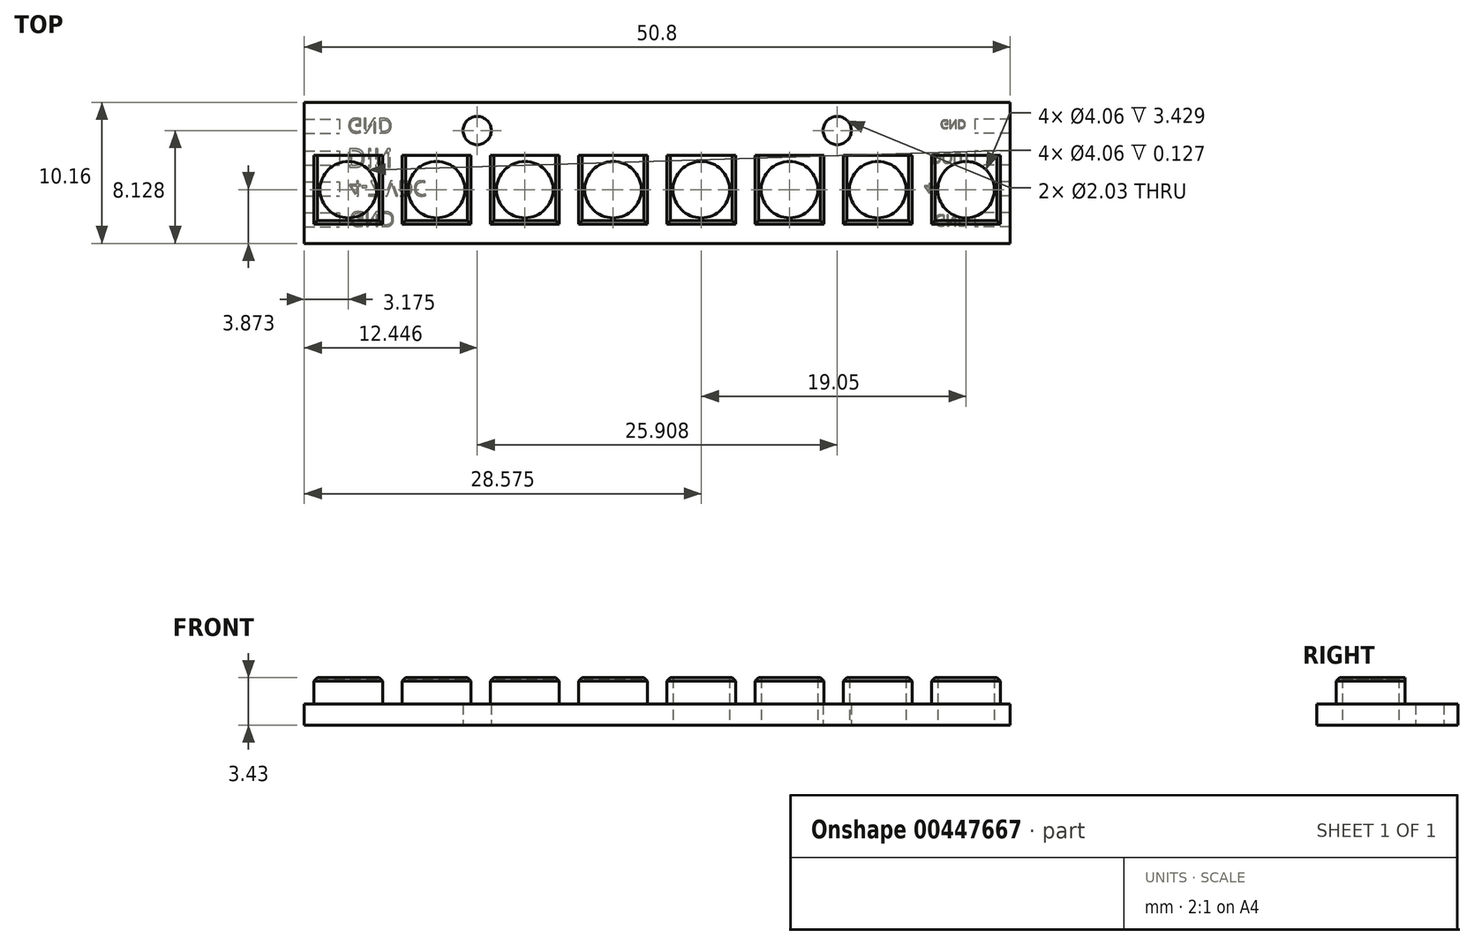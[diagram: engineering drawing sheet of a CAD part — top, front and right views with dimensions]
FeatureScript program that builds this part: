
annotation { "Feature Type Name" : "Feature", "Feature Type Description" : "" }
export const myFeature = defineFeature(function(context is Context, id is Id, definition is map)
    precondition{}
    {
        {
            var Q0;
            Q0=qCreatedBy(makeId("Top.planeOp"),FACE);
            var sketch = newSketch(context, id + "F0", { "sketchPlane" : qUnion([Q0])});
            skLineSegment(sketch, "E0.bottom", {"start": v(25.4, 5.08) * mm, "end": v(-25.4, 5.08) * mm});
            skLineSegment(sketch, "E0.top", {"start": v(25.4, -5.08) * mm, "end": v(-25.4, -5.08) * mm});
            skLineSegment(sketch, "E0.left", {"start": v(25.4, 5.08) * mm, "end": v(25.4, -5.08) * mm});
            skLineSegment(sketch, "E0.right", {"start": v(-25.4, 5.08) * mm, "end": v(-25.4, -5.08) * mm});
            skPoint(sketch, "E0.middle", {"position": v(0, 0) * mm});
            skCircle(sketch, "E1", {"center": v(-12.95, 3.05) * mm, "radius": 1.02 * mm});
            skLineSegment(sketch, "E2", {"start": v(-25.4, 1.27) * mm, "end": v(25.4, 1.27) * mm});
            skLineSegment(sketch, "E3.bottom", {"start": v(-25.4, 1.27) * mm, "end": v(-19.75, 1.27) * mm});
            skLineSegment(sketch, "E3.left", {"start": v(-25.4, 1.27) * mm, "end": v(-25.4, -3.68) * mm});
            skLineSegment(sketch, "E3.right", {"start": v(-19.75, 1.27) * mm, "end": v(-19.75, -3.68) * mm});
            skLineSegment(sketch, "E4.bottom", {"start": v(-18.35, 1.27) * mm, "end": v(-13.4, 1.27) * mm});
            skLineSegment(sketch, "E4.top", {"start": v(-18.35, -3.68) * mm, "end": v(-13.4, -3.68) * mm});
            skLineSegment(sketch, "E4.left", {"start": v(-18.35, 1.27) * mm, "end": v(-18.35, -3.68) * mm});
            skLineSegment(sketch, "E4.right", {"start": v(-13.4, 1.27) * mm, "end": v(-13.4, -3.68) * mm});
            skLineSegment(sketch, "E5.bottom", {"start": v(-12, 1.27) * mm, "end": v(-7.05, 1.27) * mm});
            skLineSegment(sketch, "E5.top", {"start": v(-12, -3.68) * mm, "end": v(-7.05, -3.68) * mm});
            skLineSegment(sketch, "E5.left", {"start": v(-12, 1.27) * mm, "end": v(-12, -3.68) * mm});
            skLineSegment(sketch, "E5.right", {"start": v(-7.05, 1.27) * mm, "end": v(-7.05, -3.68) * mm});
            skPoint(sketch, "E6.oppositeSnap0", {"position": v(-9.53, -3.68) * mm});
            skLineSegment(sketch, "E6.bottom", {"start": v(-5.65, 1.27) * mm, "end": v(-0.7, 1.27) * mm});
            skLineSegment(sketch, "E6.top", {"start": v(-5.65, -3.68) * mm, "end": v(-0.7, -3.68) * mm});
            skLineSegment(sketch, "E6.left", {"start": v(-5.65, 1.27) * mm, "end": v(-5.65, -3.68) * mm});
            skLineSegment(sketch, "E6.right", {"start": v(-0.7, 1.27) * mm, "end": v(-0.7, -3.68) * mm});
            skCircle(sketch, "E7.MirrorC", {"center": v(12.95, 3.05) * mm, "radius": 1.02 * mm});
            skLineSegment(sketch, "E8.MirrorCS", {"start": v(18.35, -3.68) * mm, "end": v(13.4, -3.68) * mm});
            skLineSegment(sketch, "E9.MirrorCS", {"start": v(13.4, 1.27) * mm, "end": v(13.4, -3.68) * mm});
            skLineSegment(sketch, "E10.MirrorCS", {"start": v(18.35, 1.27) * mm, "end": v(18.35, -3.68) * mm});
            skLineSegment(sketch, "E11.MirrorCS", {"start": v(18.35, 1.27) * mm, "end": v(13.4, 1.27) * mm});
            skLineSegment(sketch, "E12.MirrorCS", {"start": v(19.75, 1.27) * mm, "end": v(19.75, -3.68) * mm});
            skLineSegment(sketch, "E13.MirrorCS", {"start": v(25.4, 1.27) * mm, "end": v(19.75, 1.27) * mm});
            skLineSegment(sketch, "E14.MirrorCS", {"start": v(25.4, 1.27) * mm, "end": v(-25.4, 1.27) * mm});
            skLineSegment(sketch, "E15.MirrorCS", {"start": v(12, 1.27) * mm, "end": v(12, -3.68) * mm});
            skLineSegment(sketch, "E16.MirrorCS", {"start": v(12, -3.68) * mm, "end": v(7.05, -3.68) * mm});
            skLineSegment(sketch, "E17.MirrorCS", {"start": v(7.05, 1.27) * mm, "end": v(7.05, -3.68) * mm});
            skLineSegment(sketch, "E18.MirrorCS", {"start": v(5.65, 1.27) * mm, "end": v(5.65, -3.68) * mm});
            skLineSegment(sketch, "E19.MirrorCS", {"start": v(5.65, 1.27) * mm, "end": v(0.7, 1.27) * mm});
            skLineSegment(sketch, "E20.MirrorCS", {"start": v(5.65, -3.68) * mm, "end": v(0.7, -3.68) * mm});
            skLineSegment(sketch, "E21.MirrorCS", {"start": v(0.7, 1.27) * mm, "end": v(0.7, -3.68) * mm});
            skPoint(sketch, "E22.centerSnap0", {"position": v(-15.88, 1.27) * mm});
            skPoint(sketch, "E23.centerSnap0", {"position": v(-9.53, 1.27) * mm});
            skPoint(sketch, "E24.centerSnap0", {"position": v(-3.18, 1.27) * mm});
            skLineSegment(sketch, "E25", {"start": v(-24.7, 1.27) * mm, "end": v(-24.7, -3.68) * mm});
            skLineSegment(sketch, "E26.MirrorCS", {"start": v(24.7, 1.27) * mm, "end": v(24.7, -3.68) * mm});
            skLineSegment(sketch, "E27", {"start": v(24.7, -3.68) * mm, "end": v(19.75, -3.68) * mm});
            skLineSegment(sketch, "E28", {"start": v(-24.7, -3.68) * mm, "end": v(-19.75, -3.68) * mm});
            skCircle(sketch, "E29", {"center": v(-22.23, -1.2) * mm, "radius": 2.03 * mm});
            skCircle(sketch, "E30", {"center": v(-15.88, -1.2) * mm, "radius": 2.03 * mm});
            skCircle(sketch, "E31", {"center": v(-9.53, -1.2) * mm, "radius": 2.03 * mm});
            skCircle(sketch, "E32", {"center": v(-3.18, -1.2) * mm, "radius": 2.03 * mm});
            skCircle(sketch, "E33.MirrorC", {"center": v(3.18, -1.2) * mm, "radius": 2.03 * mm});
            skCircle(sketch, "E34.MirrorC", {"center": v(9.53, -1.2) * mm, "radius": 2.03 * mm});
            skCircle(sketch, "E35.MirrorC", {"center": v(15.88, -1.2) * mm, "radius": 2.03 * mm});
            skCircle(sketch, "E36.MirrorC", {"center": v(22.23, -1.2) * mm, "radius": 2.03 * mm});
            skSolve(sketch);
        }
        {
            var Q0;
            {var subQ15=sQuery(id+"F0.wireOp",EDGE,"E0.bottom");Q0=makeQuery(id+"F0.imprint","IMPRINT",FACE,{"disambiguationData":[TD([[makeQuery(id+"F0.imprint","IMPRINT",EDGE,{"derivedFrom":subQ15}),1.0]])]});}
            var Q1;
            Q1=makeQuery(id+"F0.imprint","IMPRINT",FACE,{"disambiguationData":[TD([[makeQuery(id+"F0.imprint","IMPRINT",EDGE,{"derivedFrom":sQuery(id+"F0.wireOp",EDGE,"E5.top")}),1.0]])]});
            var Q2;
            Q2=makeQuery(id+"F0.imprint","IMPRINT",FACE,{"disambiguationData":[TD([[makeQuery(id+"F0.imprint","IMPRINT",EDGE,{"derivedFrom":sQuery(id+"F0.wireOp",EDGE,"E4.top")}),1.0]])]});
            var Q3;
            Q3=makeQuery(id+"F0.imprint","IMPRINT",FACE,{"disambiguationData":[TD([[makeQuery(id+"F0.imprint","IMPRINT",EDGE,{"derivedFrom":sQuery(id+"F0.wireOp",EDGE,"E3.top")}),1.0]])]});
            var Q4;
            Q4=makeQuery(id+"F0.imprint","IMPRINT",FACE,{"disambiguationData":[TD([[makeQuery(id+"F0.imprint","IMPRINT",EDGE,{"derivedFrom":sQuery(id+"F0.wireOp",EDGE,"E6.top")}),1.0]])]});
            var Q5;
            Q5=makeQuery(id+"F0.imprint","IMPRINT",FACE,{"disambiguationData":[TD([[makeQuery(id+"F0.imprint","IMPRINT",EDGE,{"derivedFrom":sQuery(id+"F0.wireOp",EDGE,"E18.MirrorCS")}),-1.0]])]});
            var Q6;
            {var subQ0=sQuery(id+"F0.wireOp",EDGE,"E15.MirrorCS");Q6=makeQuery(id+"F0.imprint","IMPRINT",FACE,{"disambiguationData":[TD([[makeQuery(id+"F0.imprint","IMPRINT",EDGE,{"derivedFrom":subQ0}),-1.0]])]});}
            var Q7;
            Q7=makeQuery(id+"F0.imprint","IMPRINT",FACE,{"disambiguationData":[TD([[makeQuery(id+"F0.imprint","IMPRINT",EDGE,{"derivedFrom":sQuery(id+"F0.wireOp",EDGE,"E8.MirrorCS")}),-1.0]])]});
            var Q8;
            {var subQ4=sQuery(id+"F0.wireOp",EDGE,"E12.MirrorCS");Q8=makeQuery(id+"F0.imprint","IMPRINT",FACE,{"disambiguationData":[TD([[makeQuery(id+"F0.imprint","IMPRINT",EDGE,{"derivedFrom":subQ4}),1.0]])]});}
            var Q9;
            {var subQ0=sQuery(id+"F0.wireOp",EDGE,"E22");var subQ1=makeQuery(id+"F0.imprint","INTERSECT",VERTEX,{"derivedFrom":[sQuery(id+"F0.wireOp",EDGE,"E4.right"),subQ0]});Q9=makeQuery(id+"F0.imprint","IMPRINT",FACE,{"disambiguationData":[TD([[makeQuery(id+"F0.imprint","IMPRINT",EDGE,{"disambiguationData":[TD([[subQ1,-1.0]])],"derivedFrom":subQ0}),1.0]])]});}
            var Q10;
            {var subQ0=sQuery(id+"F0.wireOp",EDGE,"UNAH1sZw-Ke5a-9nqM-yAOw-CyViDykzE4hE");var subQ1=makeQuery(id+"F0.imprint","INTERSECT",VERTEX,{"derivedFrom":[sQuery(id+"F0.wireOp",EDGE,"E3.right"),subQ0]});Q10=makeQuery(id+"F0.imprint","IMPRINT",FACE,{"disambiguationData":[TD([[makeQuery(id+"F0.imprint","IMPRINT",EDGE,{"disambiguationData":[TD([[subQ1,-1.0]])],"derivedFrom":subQ0}),1.0]])]});}
            var Q11;
            {var subQ1=sQuery(id+"F0.wireOp",EDGE,"E3.left");var subQ3=sQuery(id+"F0.wireOp",EDGE,"UNAH1sZw-Ke5a-9nqM-yAOw-CyViDykzE4hE");var subQ4=makeQuery(id+"F0.imprint","INTERSECT",VERTEX,{"derivedFrom":[subQ1,subQ3]});Q11=makeQuery(id+"F0.imprint","IMPRINT",FACE,{"disambiguationData":[TD([[makeQuery(id+"F0.imprint","IMPRINT",EDGE,{"disambiguationData":[TD([[subQ4,1.0]])],"derivedFrom":subQ3}),-1.0]])]});}
            var Q12;
            {var subQ0=sQuery(id+"F0.wireOp",EDGE,"E14.MirrorCS");var subQ1=sQuery(id+"F0.wireOp",EDGE,"E3.right");var subQ2=makeQuery(id+"F0.imprint","INTERSECT",VERTEX,{"derivedFrom":[subQ1,subQ0]});Q12=makeQuery(id+"F0.imprint","IMPRINT",FACE,{"disambiguationData":[TD([[makeQuery(id+"F0.imprint","IMPRINT",EDGE,{"disambiguationData":[TD([[subQ2,-1.0]])],"derivedFrom":subQ1}),-1.0]])]});}
            var Q13;
            {var subQ0=sQuery(id+"F0.wireOp",EDGE,"E14.MirrorCS");var subQ1=sQuery(id+"F0.wireOp",EDGE,"E4.left");var subQ2=makeQuery(id+"F0.imprint","INTERSECT",VERTEX,{"derivedFrom":[subQ1,subQ0]});Q13=makeQuery(id+"F0.imprint","IMPRINT",FACE,{"disambiguationData":[TD([[makeQuery(id+"F0.imprint","IMPRINT",EDGE,{"disambiguationData":[TD([[subQ2,-1.0]])],"derivedFrom":subQ1}),1.0]])]});}
            var Q14;
            {var subQ52=sQuery(id+"F0.wireOp",EDGE,"E0.top");Q14=makeQuery(id+"F0.imprint","IMPRINT",FACE,{"disambiguationData":[TD([[makeQuery(id+"F0.imprint","IMPRINT",EDGE,{"derivedFrom":subQ52}),-1.0]])]});}
            var Q15;
            {var subQ0=sQuery(id+"F0.wireOp",EDGE,"E14.MirrorCS");var subQ1=sQuery(id+"F0.wireOp",EDGE,"E4.right");var subQ2=makeQuery(id+"F0.imprint","INTERSECT",VERTEX,{"derivedFrom":[subQ1,subQ0]});Q15=makeQuery(id+"F0.imprint","IMPRINT",FACE,{"disambiguationData":[TD([[makeQuery(id+"F0.imprint","IMPRINT",EDGE,{"disambiguationData":[TD([[subQ2,-1.0]])],"derivedFrom":subQ1}),-1.0]])]});}
            var Q16;
            {var subQ0=sQuery(id+"F0.wireOp",EDGE,"E23");var subQ1=makeQuery(id+"F0.imprint","INTERSECT",VERTEX,{"derivedFrom":[sQuery(id+"F0.wireOp",EDGE,"E5.right"),subQ0]});Q16=makeQuery(id+"F0.imprint","IMPRINT",FACE,{"disambiguationData":[TD([[makeQuery(id+"F0.imprint","IMPRINT",EDGE,{"disambiguationData":[TD([[subQ1,-1.0]])],"derivedFrom":subQ0}),1.0]])]});}
            var Q17;
            {var subQ0=sQuery(id+"F0.wireOp",EDGE,"E14.MirrorCS");var subQ1=sQuery(id+"F0.wireOp",EDGE,"E5.left");var subQ2=makeQuery(id+"F0.imprint","INTERSECT",VERTEX,{"derivedFrom":[subQ1,subQ0]});Q17=makeQuery(id+"F0.imprint","IMPRINT",FACE,{"disambiguationData":[TD([[makeQuery(id+"F0.imprint","IMPRINT",EDGE,{"disambiguationData":[TD([[subQ2,-1.0]])],"derivedFrom":subQ1}),1.0]])]});}
            var Q18;
            {var subQ0=sQuery(id+"F0.wireOp",EDGE,"E14.MirrorCS");var subQ1=sQuery(id+"F0.wireOp",EDGE,"E5.right");var subQ2=makeQuery(id+"F0.imprint","INTERSECT",VERTEX,{"derivedFrom":[subQ1,subQ0]});Q18=makeQuery(id+"F0.imprint","IMPRINT",FACE,{"disambiguationData":[TD([[makeQuery(id+"F0.imprint","IMPRINT",EDGE,{"disambiguationData":[TD([[subQ2,-1.0]])],"derivedFrom":subQ1}),-1.0]])]});}
            var Q19;
            {var subQ0=sQuery(id+"F0.wireOp",EDGE,"E24");var subQ1=makeQuery(id+"F0.imprint","INTERSECT",VERTEX,{"derivedFrom":[sQuery(id+"F0.wireOp",EDGE,"E6.right"),subQ0]});Q19=makeQuery(id+"F0.imprint","IMPRINT",FACE,{"disambiguationData":[TD([[makeQuery(id+"F0.imprint","IMPRINT",EDGE,{"disambiguationData":[TD([[subQ1,-1.0]])],"derivedFrom":subQ0}),1.0]])]});}
            var Q20;
            {var subQ0=sQuery(id+"F0.wireOp",EDGE,"E14.MirrorCS");var subQ1=sQuery(id+"F0.wireOp",EDGE,"E6.left");var subQ2=makeQuery(id+"F0.imprint","INTERSECT",VERTEX,{"derivedFrom":[subQ1,subQ0]});Q20=makeQuery(id+"F0.imprint","IMPRINT",FACE,{"disambiguationData":[TD([[makeQuery(id+"F0.imprint","IMPRINT",EDGE,{"disambiguationData":[TD([[subQ2,-1.0]])],"derivedFrom":subQ1}),1.0]])]});}
            var Q21;
            {var subQ0=sQuery(id+"F0.wireOp",EDGE,"E14.MirrorCS");var subQ1=sQuery(id+"F0.wireOp",EDGE,"E6.right");var subQ2=makeQuery(id+"F0.imprint","INTERSECT",VERTEX,{"derivedFrom":[subQ1,subQ0]});Q21=makeQuery(id+"F0.imprint","IMPRINT",FACE,{"disambiguationData":[TD([[makeQuery(id+"F0.imprint","IMPRINT",EDGE,{"disambiguationData":[TD([[subQ2,-1.0]])],"derivedFrom":subQ1}),-1.0]])]});}
            var Q22;
            {var subQ0=sQuery(id+"F0.wireOp",EDGE,"8c9498a9-89d4-41b4-a61f-fcb31b3f8e1a0.MirrorC");var subQ1=makeQuery(id+"F0.imprint","INTERSECT",VERTEX,{"derivedFrom":[sQuery(id+"F0.wireOp",EDGE,"E19.MirrorCS"),subQ0]});Q22=makeQuery(id+"F0.imprint","IMPRINT",FACE,{"disambiguationData":[TD([[makeQuery(id+"F0.imprint","IMPRINT",EDGE,{"disambiguationData":[TD([[subQ1,1.0]])],"derivedFrom":subQ0}),-1.0]])]});}
            var Q23;
            {var subQ0=sQuery(id+"F0.wireOp",EDGE,"724678bf-c758-4b2b-ac49-fb71572171400.MirrorC");var subQ1=makeQuery(id+"F0.imprint","INTERSECT",VERTEX,{"derivedFrom":[sQuery(id+"F0.wireOp",EDGE,"E14.MirrorCS"),subQ0]});Q23=makeQuery(id+"F0.imprint","IMPRINT",FACE,{"disambiguationData":[TD([[makeQuery(id+"F0.imprint","IMPRINT",EDGE,{"disambiguationData":[TD([[subQ1,1.0]])],"derivedFrom":subQ0}),-1.0]])]});}
            var Q24;
            {var subQ0=sQuery(id+"F0.wireOp",EDGE,"96d1a491-8e30-4fa4-92a3-82973c83916c0.MirrorC");var subQ1=makeQuery(id+"F0.imprint","INTERSECT",VERTEX,{"derivedFrom":[sQuery(id+"F0.wireOp",EDGE,"E9.MirrorCS"),subQ0]});Q24=makeQuery(id+"F0.imprint","IMPRINT",FACE,{"disambiguationData":[TD([[makeQuery(id+"F0.imprint","IMPRINT",EDGE,{"disambiguationData":[TD([[subQ1,-1.0]])],"derivedFrom":subQ0}),-1.0]])]});}
            var Q25;
            {var subQ0=sQuery(id+"F0.wireOp",EDGE,"E14.MirrorCS");var subQ1=sQuery(id+"F0.wireOp",EDGE,"E9.MirrorCS");var subQ2=makeQuery(id+"F0.imprint","INTERSECT",VERTEX,{"derivedFrom":[subQ1,subQ0]});Q25=makeQuery(id+"F0.imprint","IMPRINT",FACE,{"disambiguationData":[TD([[makeQuery(id+"F0.imprint","IMPRINT",EDGE,{"disambiguationData":[TD([[subQ2,-1.0]])],"derivedFrom":subQ1}),1.0]])]});}
            var Q26;
            {var subQ0=sQuery(id+"F0.wireOp",EDGE,"E14.MirrorCS");var subQ1=sQuery(id+"F0.wireOp",EDGE,"E10.MirrorCS");var subQ2=makeQuery(id+"F0.imprint","INTERSECT",VERTEX,{"derivedFrom":[subQ1,subQ0]});Q26=makeQuery(id+"F0.imprint","IMPRINT",FACE,{"disambiguationData":[TD([[makeQuery(id+"F0.imprint","IMPRINT",EDGE,{"disambiguationData":[TD([[subQ2,-1.0]])],"derivedFrom":subQ1}),-1.0]])]});}
            var Q27;
            {var subQ0=sQuery(id+"F0.wireOp",EDGE,"dc3a0b8c-c6c2-4147-8545-72a2fc5a206e0.MirrorC");var subQ1=makeQuery(id+"F0.imprint","INTERSECT",VERTEX,{"derivedFrom":[sQuery(id+"F0.wireOp",EDGE,"E12.MirrorCS"),subQ0]});Q27=makeQuery(id+"F0.imprint","IMPRINT",FACE,{"disambiguationData":[TD([[makeQuery(id+"F0.imprint","IMPRINT",EDGE,{"disambiguationData":[TD([[subQ1,-1.0]])],"derivedFrom":subQ0}),-1.0]])]});}
            var Q28;
            {var subQ0=sQuery(id+"F0.wireOp",EDGE,"4b35c337-2ec3-4570-835e-5a8300de2a6e0.MirrorCS");var subQ1=sQuery(id+"F0.wireOp",EDGE,"E0.left");var subQ2=makeQuery(id+"F0.imprint","INTERSECT",VERTEX,{"derivedFrom":[subQ1,subQ0]});Q28=makeQuery(id+"F0.imprint","IMPRINT",FACE,{"disambiguationData":[TD([[makeQuery(id+"F0.imprint","IMPRINT",EDGE,{"disambiguationData":[TD([[subQ2,1.0]])],"derivedFrom":subQ1}),-1.0]])]});}
            var Q29;
            {var subQ0=sQuery(id+"F0.wireOp",EDGE,"E14.MirrorCS");var subQ1=sQuery(id+"F0.wireOp",EDGE,"E0.left");var subQ2=makeQuery(id+"F0.imprint","INTERSECT",VERTEX,{"derivedFrom":[subQ1,subQ0]});Q29=makeQuery(id+"F0.imprint","IMPRINT",FACE,{"disambiguationData":[TD([[makeQuery(id+"F0.imprint","IMPRINT",EDGE,{"disambiguationData":[TD([[subQ2,-1.0]])],"derivedFrom":subQ1}),-1.0]])]});}
            var Q30;
            {var subQ0=sQuery(id+"F0.wireOp",EDGE,"E17.MirrorCS");var subQ1=sQuery(id+"F0.wireOp",EDGE,"E14.MirrorCS");var subQ2=makeQuery(id+"F0.imprint","INTERSECT",VERTEX,{"derivedFrom":[subQ1,subQ0]});Q30=makeQuery(id+"F0.imprint","IMPRINT",FACE,{"disambiguationData":[TD([[makeQuery(id+"F0.imprint","IMPRINT",EDGE,{"disambiguationData":[TD([[subQ2,1.0]])],"derivedFrom":subQ1}),1.0]])]});}
            var Q31;
            {var subQ0=sQuery(id+"F0.wireOp",EDGE,"E17.MirrorCS");var subQ1=sQuery(id+"F0.wireOp",EDGE,"E16.MirrorCS");var subQ2=makeQuery(id+"F0.imprint","INTERSECT",VERTEX,{"derivedFrom":[subQ1,subQ0]});Q31=makeQuery(id+"F0.imprint","IMPRINT",FACE,{"disambiguationData":[TD([[makeQuery(id+"F0.imprint","IMPRINT",EDGE,{"disambiguationData":[TD([[subQ2,1.0]])],"derivedFrom":subQ1}),-1.0]])]});}
            var Q32;
            {var subQ0=sQuery(id+"F0.wireOp",EDGE,"E21.MirrorCS");var subQ1=sQuery(id+"F0.wireOp",EDGE,"E20.MirrorCS");var subQ2=makeQuery(id+"F0.imprint","INTERSECT",VERTEX,{"derivedFrom":[subQ1,subQ0]});Q32=makeQuery(id+"F0.imprint","IMPRINT",FACE,{"disambiguationData":[TD([[makeQuery(id+"F0.imprint","IMPRINT",EDGE,{"disambiguationData":[TD([[subQ2,1.0]])],"derivedFrom":subQ1}),-1.0]])]});}
            var Q33;
            {var subQ1=sQuery(id+"F0.wireOp",EDGE,"E19.MirrorCS");var subQ3=sQuery(id+"F0.wireOp",EDGE,"8c9498a9-89d4-41b4-a61f-fcb31b3f8e1a0.MirrorC");var subQ4=makeQuery(id+"F0.imprint","INTERSECT",VERTEX,{"derivedFrom":[subQ1,subQ3]});Q33=makeQuery(id+"F0.imprint","IMPRINT",FACE,{"disambiguationData":[TD([[makeQuery(id+"F0.imprint","IMPRINT",EDGE,{"disambiguationData":[TD([[subQ4,1.0]])],"derivedFrom":subQ3}),1.0]])]});}
            var Q34;
            {var subQ0=sQuery(id+"F0.wireOp",EDGE,"E28");var subQ1=sQuery(id+"F0.wireOp",EDGE,"E3.right");var subQ2=makeQuery(id+"F0.imprint","INTERSECT",VERTEX,{"derivedFrom":[subQ1,subQ0]});Q34=makeQuery(id+"F0.imprint","IMPRINT",FACE,{"disambiguationData":[TD([[makeQuery(id+"F0.imprint","IMPRINT",EDGE,{"disambiguationData":[TD([[subQ2,1.0]])],"derivedFrom":subQ1}),-1.0]])]});}
            var Q35;
            {var subQ0=sQuery(id+"F0.wireOp",EDGE,"1PWdEQUw-wEJ5-cKNr-TaBA-1jAVnnhFksSZ");var subQ1=makeQuery(id+"F0.imprint","INTERSECT",VERTEX,{"derivedFrom":[sQuery(id+"F0.wireOp",EDGE,"E3.right"),subQ0]});Q35=makeQuery(id+"F0.imprint","IMPRINT",FACE,{"disambiguationData":[TD([[makeQuery(id+"F0.imprint","IMPRINT",EDGE,{"disambiguationData":[TD([[subQ1,-1.0]])],"derivedFrom":subQ0}),1.0]])]});}
            var Q36;
            {var subQ0=sQuery(id+"F0.wireOp",EDGE,"E25");var subQ1=sQuery(id+"F0.wireOp",EDGE,"E14.MirrorCS");var subQ2=makeQuery(id+"F0.imprint","INTERSECT",VERTEX,{"derivedFrom":[subQ1,subQ0]});Q36=makeQuery(id+"F0.imprint","IMPRINT",FACE,{"disambiguationData":[TD([[makeQuery(id+"F0.imprint","IMPRINT",EDGE,{"disambiguationData":[TD([[subQ2,1.0]])],"derivedFrom":subQ1}),1.0]])]});}
            var Q37;
            {var subQ0=sQuery(id+"F0.wireOp",EDGE,"E28");var subQ1=sQuery(id+"F0.wireOp",EDGE,"E25");var subQ2=makeQuery(id+"F0.imprint","INTERSECT",VERTEX,{"derivedFrom":[subQ1,subQ0]});Q37=makeQuery(id+"F0.imprint","IMPRINT",FACE,{"disambiguationData":[TD([[makeQuery(id+"F0.imprint","IMPRINT",EDGE,{"disambiguationData":[TD([[subQ2,1.0]])],"derivedFrom":subQ1}),1.0]])]});}
            var Q38;
            {var subQ0=sQuery(id+"F0.wireOp",EDGE,"3694e821-6fd0-43f0-b6cd-c99c7b0efe270.MirrorC");var subQ1=makeQuery(id+"F0.imprint","INTERSECT",VERTEX,{"derivedFrom":[sQuery(id+"F0.wireOp",EDGE,"E12.MirrorCS"),subQ0]});Q38=makeQuery(id+"F0.imprint","IMPRINT",FACE,{"disambiguationData":[TD([[makeQuery(id+"F0.imprint","IMPRINT",EDGE,{"disambiguationData":[TD([[subQ1,-1.0]])],"derivedFrom":subQ0}),-1.0]])]});}
            var Q39;
            {var subQ0=sQuery(id+"F0.wireOp",EDGE,"E26.MirrorCS");var subQ1=sQuery(id+"F0.wireOp",EDGE,"E14.MirrorCS");var subQ2=makeQuery(id+"F0.imprint","INTERSECT",VERTEX,{"derivedFrom":[subQ1,subQ0]});Q39=makeQuery(id+"F0.imprint","IMPRINT",FACE,{"disambiguationData":[TD([[makeQuery(id+"F0.imprint","IMPRINT",EDGE,{"disambiguationData":[TD([[subQ2,-1.0]])],"derivedFrom":subQ1}),1.0]])]});}
            var Q40;
            {var subQ0=sQuery(id+"F0.wireOp",EDGE,"E26.MirrorCS");var subQ1=sQuery(id+"F0.wireOp",EDGE,"3694e821-6fd0-43f0-b6cd-c99c7b0efe270.MirrorC");var subQ2=makeQuery(id+"F0.imprint","INTERSECT",VERTEX,{"derivedFrom":[subQ1,subQ0]});Q40=makeQuery(id+"F0.imprint","IMPRINT",FACE,{"disambiguationData":[TD([[makeQuery(id+"F0.imprint","IMPRINT",EDGE,{"disambiguationData":[TD([[subQ2,-1.0]])],"derivedFrom":subQ1}),1.0]])]});}
            var Q41;
            Q41=makeQuery(id+"F0.imprint","IMPRINT",FACE,{"disambiguationData":[TD([[makeQuery(id+"F0.imprint","IMPRINT",EDGE,{"derivedFrom":sQuery(id+"F0.wireOp",EDGE,"E29")}),1.0]])]});
            var Q42;
            Q42=makeQuery(id+"F0.imprint","IMPRINT",FACE,{"disambiguationData":[TD([[makeQuery(id+"F0.imprint","IMPRINT",EDGE,{"derivedFrom":sQuery(id+"F0.wireOp",EDGE,"E30")}),1.0]])]});
            var Q43;
            Q43=makeQuery(id+"F0.imprint","IMPRINT",FACE,{"disambiguationData":[TD([[makeQuery(id+"F0.imprint","IMPRINT",EDGE,{"derivedFrom":sQuery(id+"F0.wireOp",EDGE,"E31")}),1.0]])]});
            var Q44;
            Q44=makeQuery(id+"F0.imprint","IMPRINT",FACE,{"disambiguationData":[TD([[makeQuery(id+"F0.imprint","IMPRINT",EDGE,{"derivedFrom":sQuery(id+"F0.wireOp",EDGE,"E33.MirrorC")}),-1.0]])]});
            var Q45;
            Q45=makeQuery(id+"F0.imprint","IMPRINT",FACE,{"disambiguationData":[TD([[makeQuery(id+"F0.imprint","IMPRINT",EDGE,{"derivedFrom":sQuery(id+"F0.wireOp",EDGE,"E34.MirrorC")}),-1.0]])]});
            var Q46;
            Q46=makeQuery(id+"F0.imprint","IMPRINT",FACE,{"disambiguationData":[TD([[makeQuery(id+"F0.imprint","IMPRINT",EDGE,{"derivedFrom":sQuery(id+"F0.wireOp",EDGE,"E32")}),1.0]])]});
            var Q47;
            Q47=makeQuery(id+"F0.imprint","IMPRINT",FACE,{"disambiguationData":[TD([[makeQuery(id+"F0.imprint","IMPRINT",EDGE,{"derivedFrom":sQuery(id+"F0.wireOp",EDGE,"E35.MirrorC")}),-1.0]])]});
            var Q48;
            Q48=makeQuery(id+"F0.imprint","IMPRINT",FACE,{"disambiguationData":[TD([[makeQuery(id+"F0.imprint","IMPRINT",EDGE,{"derivedFrom":sQuery(id+"F0.wireOp",EDGE,"E36.MirrorC")}),-1.0]])]});
            extrude(context, id + "F1", {"entities" : qUnion([Q0, Q1, Q2, Q3, Q4, Q5, Q6, Q7, Q8, Q9, Q10, Q11, Q12, Q13, Q14, Q15, Q16, Q17, Q18, Q19, Q20, Q21, Q22, Q23, Q24, Q25, Q26, Q27, Q28, Q29, Q30, Q31, Q32, Q33, Q34, Q35, Q36, Q37, Q38, Q39, Q40, Q41, Q42, Q43, Q44, Q45, Q46, Q47, Q48]), "endBound" : BoundingType.SYMMETRIC, "depth" : 1.52 * mm});
        }
        {
            var Q0;
            Q0=makeQuery(id+"F1.opExtrude","CAP_FACE",FACE,{"disambiguationData":[OSD([sQuery(id+"F0.wireOp",EDGE,"E0.bottom"),sQuery(id+"F0.wireOp",EDGE,"E0.top"),sQuery(id+"F0.wireOp",EDGE,"E0.left"),sQuery(id+"F0.wireOp",EDGE,"E0.right"),sQuery(id+"F0.wireOp",EDGE,"E1"),sQuery(id+"F0.wireOp",EDGE,"E3.left"),sQuery(id+"F0.wireOp",EDGE,"E7.MirrorC")])],"isStart":true});
            var sketch = newSketch(context, id + "F2", { "sketchPlane" : qUnion([Q0])});
            skLineSegment(sketch, "E37.bottom", {"start": v(25.4, -3.87) * mm, "end": v(22.86, -3.87) * mm});
            skLineSegment(sketch, "E37.top", {"start": v(25.4, -2.86) * mm, "end": v(22.86, -2.86) * mm});
            skLineSegment(sketch, "E37.left", {"start": v(25.4, -3.87) * mm, "end": v(25.4, -2.86) * mm});
            skLineSegment(sketch, "E37.right", {"start": v(22.86, -3.87) * mm, "end": v(22.86, -2.86) * mm});
            skLineSegment(sketch, "E38.bottom", {"start": v(25.4, -1.59) * mm, "end": v(22.86, -1.59) * mm});
            skLineSegment(sketch, "E38.top", {"start": v(25.4, -0.57) * mm, "end": v(22.86, -0.57) * mm});
            skLineSegment(sketch, "E38.left", {"start": v(25.4, -1.59) * mm, "end": v(25.4, -0.57) * mm});
            skLineSegment(sketch, "E38.right", {"start": v(22.86, -1.59) * mm, "end": v(22.86, -0.57) * mm});
            skLineSegment(sketch, "E39.bottom", {"start": v(25.4, 0.64) * mm, "end": v(22.86, 0.64) * mm});
            skLineSegment(sketch, "E39.top", {"start": v(25.4, 1.65) * mm, "end": v(22.86, 1.65) * mm});
            skLineSegment(sketch, "E39.left", {"start": v(25.4, 0.64) * mm, "end": v(25.4, 1.65) * mm});
            skLineSegment(sketch, "E39.right", {"start": v(22.86, 0.64) * mm, "end": v(22.86, 1.65) * mm});
            skLineSegment(sketch, "E40.bottom", {"start": v(25.4, 2.86) * mm, "end": v(22.86, 2.86) * mm});
            skLineSegment(sketch, "E40.top", {"start": v(25.4, 3.87) * mm, "end": v(22.86, 3.87) * mm});
            skLineSegment(sketch, "E40.left", {"start": v(25.4, 2.86) * mm, "end": v(25.4, 3.87) * mm});
            skLineSegment(sketch, "E40.right", {"start": v(22.86, 2.86) * mm, "end": v(22.86, 3.87) * mm});
            skLineSegment(sketch, "E41.MirrorCS", {"start": v(22.86, -3.87) * mm, "end": v(22.86, -4.89) * mm});
            skLineSegment(sketch, "E42.MirrorCS", {"start": v(-25.4, -3.87) * mm, "end": v(-22.86, -3.87) * mm});
            skLineSegment(sketch, "E43.MirrorCS", {"start": v(-22.86, -3.87) * mm, "end": v(-22.86, -2.86) * mm});
            skLineSegment(sketch, "E44.MirrorCS", {"start": v(-25.4, -2.86) * mm, "end": v(-22.86, -2.86) * mm});
            skLineSegment(sketch, "E45.MirrorCS", {"start": v(-25.4, -1.59) * mm, "end": v(-22.86, -1.59) * mm});
            skLineSegment(sketch, "E46.MirrorCS", {"start": v(-22.86, -1.59) * mm, "end": v(-22.86, -0.57) * mm});
            skLineSegment(sketch, "E47.MirrorCS", {"start": v(-25.4, -0.57) * mm, "end": v(-22.86, -0.57) * mm});
            skLineSegment(sketch, "E48.MirrorCS", {"start": v(-25.4, 0.64) * mm, "end": v(-22.86, 0.64) * mm});
            skLineSegment(sketch, "E49.MirrorCS", {"start": v(-22.86, 0.64) * mm, "end": v(-22.86, 1.65) * mm});
            skLineSegment(sketch, "E50.MirrorCS", {"start": v(-25.4, 1.65) * mm, "end": v(-22.86, 1.65) * mm});
            skLineSegment(sketch, "E51.MirrorCS", {"start": v(-22.86, 2.86) * mm, "end": v(-22.86, 3.87) * mm});
            skLineSegment(sketch, "E52.MirrorCS", {"start": v(-25.4, 2.86) * mm, "end": v(-22.86, 2.86) * mm});
            skLineSegment(sketch, "E53.MirrorCS", {"start": v(-25.4, 3.87) * mm, "end": v(-22.86, 3.87) * mm});
            skText(sketch, "E54", { "text": "GND", "fontName": "OpenSans-Regular.ttf"});
            skText(sketch, "E55", { "text": "DOUT", "fontName": "OpenSans-Regular.ttf"});
            skText(sketch, "E56", { "text": "4-7 VDC", "fontName": "OpenSans-Regular.ttf"});
            skText(sketch, "E57", { "text": "GND", "fontName": "OpenSans-Regular.ttf"});
            skText(sketch, "E58", { "text": "GND\n", "fontName": "OpenSans-Regular.ttf"});
            skText(sketch, "E59", { "text": "DIN", "fontName": "OpenSans-Regular.ttf"});
            skText(sketch, "E60", { "text": "4-7 VDC", "fontName": "OpenSans-Regular.ttf"});
            skText(sketch, "E61", { "text": "GND", "fontName": "OpenSans-Regular.ttf"});
            const initialGuessF2  = {"E54": [0.02037, -0.0038, 1, 0, 0.0006], "E55": [0.01973, -0.00143, 1, 0, 0.00073], "E56": [0.01922, 0.00078, 1, 0, 0.00065], "E57": [0.01995, 0.00303, 1, 0, 0.0008], "E58": [-0.02228, -0.00392, 1, 0, 0.00105], "E59": [-0.02233, -0.00174, 1, 0, 0.00135], "E60": [-0.02218, 0.00058, 1, 0, 0.00109], "E61": [-0.02214, 0.0028, 1, 0, 0.00106]};
            skSetInitialGuess(sketch, initialGuessF2);
            skSolve(sketch);
        }
        {
            var Q0;
            Q0=qSketchRegion(id+"F2",true);
            var Q1;
            Q1=makeQuery(id+"F2.imprint","IMPRINT",FACE,{"disambiguationData":[TD([[makeQuery(id+"F2.imprint","IMPRINT",EDGE,{"derivedFrom":sQuery(id+"F2.wireOp",EDGE,"E51.MirrorCS")}),1.0]])]});
            var Q2;
            {var subQ0=sQuery(id+"F2.wireOp",EDGE,"E48.MirrorCS");Q2=makeQuery(id+"F2.imprint","IMPRINT",FACE,{"disambiguationData":[TD([[makeQuery(id+"F2.imprint","IMPRINT",EDGE,{"derivedFrom":subQ0}),1.0]])]});}
            var Q3;
            {var subQ0=sQuery(id+"F2.wireOp",EDGE,"E45.MirrorCS");Q3=makeQuery(id+"F2.imprint","IMPRINT",FACE,{"disambiguationData":[TD([[makeQuery(id+"F2.imprint","IMPRINT",EDGE,{"derivedFrom":subQ0}),1.0]])]});}
            var Q4;
            {var subQ0=sQuery(id+"F2.wireOp",EDGE,"E42.MirrorCS");Q4=makeQuery(id+"F2.imprint","IMPRINT",FACE,{"disambiguationData":[TD([[makeQuery(id+"F2.imprint","IMPRINT",EDGE,{"derivedFrom":subQ0}),1.0]])]});}
            extrude(context, id + "F3", {"entities" : qUnion([Q0, Q1, Q2, Q3, Q4]), "operationType" : NewBodyOperationType.REMOVE, "oppositeDirection" : true, "depth" : 0.01 * mm});
        }
        {
            var Q0;
            {var subQ0=sQuery(id+"F0.wireOp",EDGE,"E26.MirrorCS");var subQ1=sQuery(id+"F0.wireOp",EDGE,"E14.MirrorCS");var subQ2=makeQuery(id+"F0.imprint","INTERSECT",VERTEX,{"derivedFrom":[subQ1,subQ0]});Q0=makeQuery(id+"F0.imprint","IMPRINT",FACE,{"disambiguationData":[TD([[makeQuery(id+"F0.imprint","IMPRINT",EDGE,{"disambiguationData":[TD([[subQ2,-1.0]])],"derivedFrom":subQ1}),1.0]])]});}
            var Q1;
            {var subQ0=sQuery(id+"F0.wireOp",EDGE,"E26.MirrorCS");var subQ1=sQuery(id+"F0.wireOp",EDGE,"3694e821-6fd0-43f0-b6cd-c99c7b0efe270.MirrorC");var subQ2=makeQuery(id+"F0.imprint","INTERSECT",VERTEX,{"derivedFrom":[subQ1,subQ0]});Q1=makeQuery(id+"F0.imprint","IMPRINT",FACE,{"disambiguationData":[TD([[makeQuery(id+"F0.imprint","IMPRINT",EDGE,{"disambiguationData":[TD([[subQ2,-1.0]])],"derivedFrom":subQ1}),1.0]])]});}
            var Q2;
            {var subQ0=sQuery(id+"F0.wireOp",EDGE,"E27");var subQ1=sQuery(id+"F0.wireOp",EDGE,"E12.MirrorCS");var subQ2=makeQuery(id+"F0.imprint","INTERSECT",VERTEX,{"derivedFrom":[subQ1,subQ0]});Q2=makeQuery(id+"F0.imprint","IMPRINT",FACE,{"disambiguationData":[TD([[makeQuery(id+"F0.imprint","IMPRINT",EDGE,{"disambiguationData":[TD([[subQ2,1.0]])],"derivedFrom":subQ1}),1.0]])]});}
            var Q3;
            {var subQ0=sQuery(id+"F0.wireOp",EDGE,"E14.MirrorCS");var subQ1=sQuery(id+"F0.wireOp",EDGE,"E12.MirrorCS");var subQ2=makeQuery(id+"F0.imprint","INTERSECT",VERTEX,{"derivedFrom":[subQ1,subQ0]});Q3=makeQuery(id+"F0.imprint","IMPRINT",FACE,{"disambiguationData":[TD([[makeQuery(id+"F0.imprint","IMPRINT",EDGE,{"disambiguationData":[TD([[subQ2,-1.0]])],"derivedFrom":subQ1}),1.0]])]});}
            var Q4;
            {var subQ0=sQuery(id+"F0.wireOp",EDGE,"E14.MirrorCS");var subQ1=sQuery(id+"F0.wireOp",EDGE,"E10.MirrorCS");var subQ2=makeQuery(id+"F0.imprint","INTERSECT",VERTEX,{"derivedFrom":[subQ1,subQ0]});Q4=makeQuery(id+"F0.imprint","IMPRINT",FACE,{"disambiguationData":[TD([[makeQuery(id+"F0.imprint","IMPRINT",EDGE,{"disambiguationData":[TD([[subQ2,-1.0]])],"derivedFrom":subQ1}),-1.0]])]});}
            var Q5;
            {var subQ0=sQuery(id+"F0.wireOp",EDGE,"E10.MirrorCS");var subQ1=sQuery(id+"F0.wireOp",EDGE,"E8.MirrorCS");var subQ2=makeQuery(id+"F0.imprint","INTERSECT",VERTEX,{"derivedFrom":[subQ1,subQ0]});Q5=makeQuery(id+"F0.imprint","IMPRINT",FACE,{"disambiguationData":[TD([[makeQuery(id+"F0.imprint","IMPRINT",EDGE,{"disambiguationData":[TD([[subQ2,-1.0]])],"derivedFrom":subQ1}),-1.0]])]});}
            var Q6;
            {var subQ0=sQuery(id+"F0.wireOp",EDGE,"E9.MirrorCS");var subQ1=sQuery(id+"F0.wireOp",EDGE,"E8.MirrorCS");var subQ2=makeQuery(id+"F0.imprint","INTERSECT",VERTEX,{"derivedFrom":[subQ1,subQ0]});Q6=makeQuery(id+"F0.imprint","IMPRINT",FACE,{"disambiguationData":[TD([[makeQuery(id+"F0.imprint","IMPRINT",EDGE,{"disambiguationData":[TD([[subQ2,1.0]])],"derivedFrom":subQ1}),-1.0]])]});}
            var Q7;
            {var subQ0=sQuery(id+"F0.wireOp",EDGE,"E14.MirrorCS");var subQ1=sQuery(id+"F0.wireOp",EDGE,"E9.MirrorCS");var subQ2=makeQuery(id+"F0.imprint","INTERSECT",VERTEX,{"derivedFrom":[subQ1,subQ0]});Q7=makeQuery(id+"F0.imprint","IMPRINT",FACE,{"disambiguationData":[TD([[makeQuery(id+"F0.imprint","IMPRINT",EDGE,{"disambiguationData":[TD([[subQ2,-1.0]])],"derivedFrom":subQ1}),1.0]])]});}
            var Q8;
            {var subQ0=sQuery(id+"F0.wireOp",EDGE,"E15.MirrorCS");var subQ1=sQuery(id+"F0.wireOp",EDGE,"E14.MirrorCS");var subQ2=makeQuery(id+"F0.imprint","INTERSECT",VERTEX,{"derivedFrom":[subQ1,subQ0]});Q8=makeQuery(id+"F0.imprint","IMPRINT",FACE,{"disambiguationData":[TD([[makeQuery(id+"F0.imprint","IMPRINT",EDGE,{"disambiguationData":[TD([[subQ2,-1.0]])],"derivedFrom":subQ1}),1.0]])]});}
            var Q9;
            {var subQ0=sQuery(id+"F0.wireOp",EDGE,"E16.MirrorCS");var subQ1=sQuery(id+"F0.wireOp",EDGE,"E15.MirrorCS");var subQ2=makeQuery(id+"F0.imprint","INTERSECT",VERTEX,{"derivedFrom":[subQ1,subQ0]});Q9=makeQuery(id+"F0.imprint","IMPRINT",FACE,{"disambiguationData":[TD([[makeQuery(id+"F0.imprint","IMPRINT",EDGE,{"disambiguationData":[TD([[subQ2,1.0]])],"derivedFrom":subQ1}),-1.0]])]});}
            var Q10;
            {var subQ0=sQuery(id+"F0.wireOp",EDGE,"E17.MirrorCS");var subQ1=sQuery(id+"F0.wireOp",EDGE,"E14.MirrorCS");var subQ2=makeQuery(id+"F0.imprint","INTERSECT",VERTEX,{"derivedFrom":[subQ1,subQ0]});Q10=makeQuery(id+"F0.imprint","IMPRINT",FACE,{"disambiguationData":[TD([[makeQuery(id+"F0.imprint","IMPRINT",EDGE,{"disambiguationData":[TD([[subQ2,1.0]])],"derivedFrom":subQ1}),1.0]])]});}
            var Q11;
            {var subQ0=sQuery(id+"F0.wireOp",EDGE,"E17.MirrorCS");var subQ1=sQuery(id+"F0.wireOp",EDGE,"E16.MirrorCS");var subQ2=makeQuery(id+"F0.imprint","INTERSECT",VERTEX,{"derivedFrom":[subQ1,subQ0]});Q11=makeQuery(id+"F0.imprint","IMPRINT",FACE,{"disambiguationData":[TD([[makeQuery(id+"F0.imprint","IMPRINT",EDGE,{"disambiguationData":[TD([[subQ2,1.0]])],"derivedFrom":subQ1}),-1.0]])]});}
            var Q12;
            {var subQ0=sQuery(id+"F0.wireOp",EDGE,"E20.MirrorCS");var subQ1=sQuery(id+"F0.wireOp",EDGE,"E18.MirrorCS");var subQ2=makeQuery(id+"F0.imprint","INTERSECT",VERTEX,{"derivedFrom":[subQ1,subQ0]});Q12=makeQuery(id+"F0.imprint","IMPRINT",FACE,{"disambiguationData":[TD([[makeQuery(id+"F0.imprint","IMPRINT",EDGE,{"disambiguationData":[TD([[subQ2,1.0]])],"derivedFrom":subQ1}),-1.0]])]});}
            var Q13;
            {var subQ1=sQuery(id+"F0.wireOp",EDGE,"E18.MirrorCS");var subQ3=sQuery(id+"F0.wireOp",EDGE,"8c9498a9-89d4-41b4-a61f-fcb31b3f8e1a0.MirrorC");var subQ4=makeQuery(id+"F0.imprint","INTERSECT",VERTEX,{"derivedFrom":[subQ1,subQ3]});Q13=makeQuery(id+"F0.imprint","IMPRINT",FACE,{"disambiguationData":[TD([[makeQuery(id+"F0.imprint","IMPRINT",EDGE,{"disambiguationData":[TD([[subQ4,1.0]])],"derivedFrom":subQ3}),1.0]])]});}
            var Q14;
            {var subQ1=sQuery(id+"F0.wireOp",EDGE,"E19.MirrorCS");var subQ3=sQuery(id+"F0.wireOp",EDGE,"8c9498a9-89d4-41b4-a61f-fcb31b3f8e1a0.MirrorC");var subQ4=makeQuery(id+"F0.imprint","INTERSECT",VERTEX,{"derivedFrom":[subQ1,subQ3]});Q14=makeQuery(id+"F0.imprint","IMPRINT",FACE,{"disambiguationData":[TD([[makeQuery(id+"F0.imprint","IMPRINT",EDGE,{"disambiguationData":[TD([[subQ4,1.0]])],"derivedFrom":subQ3}),1.0]])]});}
            var Q15;
            {var subQ0=sQuery(id+"F0.wireOp",EDGE,"E21.MirrorCS");var subQ1=sQuery(id+"F0.wireOp",EDGE,"E20.MirrorCS");var subQ2=makeQuery(id+"F0.imprint","INTERSECT",VERTEX,{"derivedFrom":[subQ1,subQ0]});Q15=makeQuery(id+"F0.imprint","IMPRINT",FACE,{"disambiguationData":[TD([[makeQuery(id+"F0.imprint","IMPRINT",EDGE,{"disambiguationData":[TD([[subQ2,1.0]])],"derivedFrom":subQ1}),-1.0]])]});}
            var Q16;
            {var subQ0=sQuery(id+"F0.wireOp",EDGE,"E14.MirrorCS");var subQ1=sQuery(id+"F0.wireOp",EDGE,"E6.right");var subQ2=makeQuery(id+"F0.imprint","INTERSECT",VERTEX,{"derivedFrom":[subQ1,subQ0]});Q16=makeQuery(id+"F0.imprint","IMPRINT",FACE,{"disambiguationData":[TD([[makeQuery(id+"F0.imprint","IMPRINT",EDGE,{"disambiguationData":[TD([[subQ2,-1.0]])],"derivedFrom":subQ1}),-1.0]])]});}
            var Q17;
            {var subQ0=sQuery(id+"F0.wireOp",EDGE,"E6.right");var subQ1=sQuery(id+"F0.wireOp",EDGE,"E6.top");var subQ2=makeQuery(id+"F0.imprint","INTERSECT",VERTEX,{"derivedFrom":[subQ1,subQ0]});Q17=makeQuery(id+"F0.imprint","IMPRINT",FACE,{"disambiguationData":[TD([[makeQuery(id+"F0.imprint","IMPRINT",EDGE,{"disambiguationData":[TD([[subQ2,1.0]])],"derivedFrom":subQ1}),1.0]])]});}
            var Q18;
            {var subQ0=sQuery(id+"F0.wireOp",EDGE,"E6.left");var subQ1=sQuery(id+"F0.wireOp",EDGE,"E6.top");var subQ2=makeQuery(id+"F0.imprint","INTERSECT",VERTEX,{"derivedFrom":[subQ1,subQ0]});Q18=makeQuery(id+"F0.imprint","IMPRINT",FACE,{"disambiguationData":[TD([[makeQuery(id+"F0.imprint","IMPRINT",EDGE,{"disambiguationData":[TD([[subQ2,-1.0]])],"derivedFrom":subQ1}),1.0]])]});}
            var Q19;
            {var subQ0=sQuery(id+"F0.wireOp",EDGE,"E14.MirrorCS");var subQ1=sQuery(id+"F0.wireOp",EDGE,"E6.left");var subQ2=makeQuery(id+"F0.imprint","INTERSECT",VERTEX,{"derivedFrom":[subQ1,subQ0]});Q19=makeQuery(id+"F0.imprint","IMPRINT",FACE,{"disambiguationData":[TD([[makeQuery(id+"F0.imprint","IMPRINT",EDGE,{"disambiguationData":[TD([[subQ2,-1.0]])],"derivedFrom":subQ1}),1.0]])]});}
            var Q20;
            {var subQ0=sQuery(id+"F0.wireOp",EDGE,"E14.MirrorCS");var subQ1=sQuery(id+"F0.wireOp",EDGE,"E5.right");var subQ2=makeQuery(id+"F0.imprint","INTERSECT",VERTEX,{"derivedFrom":[subQ1,subQ0]});Q20=makeQuery(id+"F0.imprint","IMPRINT",FACE,{"disambiguationData":[TD([[makeQuery(id+"F0.imprint","IMPRINT",EDGE,{"disambiguationData":[TD([[subQ2,-1.0]])],"derivedFrom":subQ1}),-1.0]])]});}
            var Q21;
            {var subQ0=sQuery(id+"F0.wireOp",EDGE,"E5.right");var subQ1=sQuery(id+"F0.wireOp",EDGE,"E5.top");var subQ2=makeQuery(id+"F0.imprint","INTERSECT",VERTEX,{"derivedFrom":[subQ1,subQ0]});Q21=makeQuery(id+"F0.imprint","IMPRINT",FACE,{"disambiguationData":[TD([[makeQuery(id+"F0.imprint","IMPRINT",EDGE,{"disambiguationData":[TD([[subQ2,1.0]])],"derivedFrom":subQ1}),1.0]])]});}
            var Q22;
            {var subQ0=sQuery(id+"F0.wireOp",EDGE,"E5.left");var subQ1=sQuery(id+"F0.wireOp",EDGE,"E5.top");var subQ2=makeQuery(id+"F0.imprint","INTERSECT",VERTEX,{"derivedFrom":[subQ1,subQ0]});Q22=makeQuery(id+"F0.imprint","IMPRINT",FACE,{"disambiguationData":[TD([[makeQuery(id+"F0.imprint","IMPRINT",EDGE,{"disambiguationData":[TD([[subQ2,-1.0]])],"derivedFrom":subQ1}),1.0]])]});}
            var Q23;
            {var subQ0=sQuery(id+"F0.wireOp",EDGE,"E14.MirrorCS");var subQ1=sQuery(id+"F0.wireOp",EDGE,"E5.left");var subQ2=makeQuery(id+"F0.imprint","INTERSECT",VERTEX,{"derivedFrom":[subQ1,subQ0]});Q23=makeQuery(id+"F0.imprint","IMPRINT",FACE,{"disambiguationData":[TD([[makeQuery(id+"F0.imprint","IMPRINT",EDGE,{"disambiguationData":[TD([[subQ2,-1.0]])],"derivedFrom":subQ1}),1.0]])]});}
            var Q24;
            {var subQ0=sQuery(id+"F0.wireOp",EDGE,"E14.MirrorCS");var subQ1=sQuery(id+"F0.wireOp",EDGE,"E4.right");var subQ2=makeQuery(id+"F0.imprint","INTERSECT",VERTEX,{"derivedFrom":[subQ1,subQ0]});Q24=makeQuery(id+"F0.imprint","IMPRINT",FACE,{"disambiguationData":[TD([[makeQuery(id+"F0.imprint","IMPRINT",EDGE,{"disambiguationData":[TD([[subQ2,-1.0]])],"derivedFrom":subQ1}),-1.0]])]});}
            var Q25;
            {var subQ0=sQuery(id+"F0.wireOp",EDGE,"E4.right");var subQ1=sQuery(id+"F0.wireOp",EDGE,"E4.top");var subQ2=makeQuery(id+"F0.imprint","INTERSECT",VERTEX,{"derivedFrom":[subQ1,subQ0]});Q25=makeQuery(id+"F0.imprint","IMPRINT",FACE,{"disambiguationData":[TD([[makeQuery(id+"F0.imprint","IMPRINT",EDGE,{"disambiguationData":[TD([[subQ2,1.0]])],"derivedFrom":subQ1}),1.0]])]});}
            var Q26;
            {var subQ0=sQuery(id+"F0.wireOp",EDGE,"E4.left");var subQ1=sQuery(id+"F0.wireOp",EDGE,"E4.top");var subQ2=makeQuery(id+"F0.imprint","INTERSECT",VERTEX,{"derivedFrom":[subQ1,subQ0]});Q26=makeQuery(id+"F0.imprint","IMPRINT",FACE,{"disambiguationData":[TD([[makeQuery(id+"F0.imprint","IMPRINT",EDGE,{"disambiguationData":[TD([[subQ2,-1.0]])],"derivedFrom":subQ1}),1.0]])]});}
            var Q27;
            {var subQ0=sQuery(id+"F0.wireOp",EDGE,"E14.MirrorCS");var subQ1=sQuery(id+"F0.wireOp",EDGE,"E4.left");var subQ2=makeQuery(id+"F0.imprint","INTERSECT",VERTEX,{"derivedFrom":[subQ1,subQ0]});Q27=makeQuery(id+"F0.imprint","IMPRINT",FACE,{"disambiguationData":[TD([[makeQuery(id+"F0.imprint","IMPRINT",EDGE,{"disambiguationData":[TD([[subQ2,-1.0]])],"derivedFrom":subQ1}),1.0]])]});}
            var Q28;
            {var subQ0=sQuery(id+"F0.wireOp",EDGE,"E14.MirrorCS");var subQ1=sQuery(id+"F0.wireOp",EDGE,"E3.right");var subQ2=makeQuery(id+"F0.imprint","INTERSECT",VERTEX,{"derivedFrom":[subQ1,subQ0]});Q28=makeQuery(id+"F0.imprint","IMPRINT",FACE,{"disambiguationData":[TD([[makeQuery(id+"F0.imprint","IMPRINT",EDGE,{"disambiguationData":[TD([[subQ2,-1.0]])],"derivedFrom":subQ1}),-1.0]])]});}
            var Q29;
            {var subQ0=sQuery(id+"F0.wireOp",EDGE,"E28");var subQ1=sQuery(id+"F0.wireOp",EDGE,"E3.right");var subQ2=makeQuery(id+"F0.imprint","INTERSECT",VERTEX,{"derivedFrom":[subQ1,subQ0]});Q29=makeQuery(id+"F0.imprint","IMPRINT",FACE,{"disambiguationData":[TD([[makeQuery(id+"F0.imprint","IMPRINT",EDGE,{"disambiguationData":[TD([[subQ2,1.0]])],"derivedFrom":subQ1}),-1.0]])]});}
            var Q30;
            {var subQ0=sQuery(id+"F0.wireOp",EDGE,"E28");var subQ1=sQuery(id+"F0.wireOp",EDGE,"E25");var subQ2=makeQuery(id+"F0.imprint","INTERSECT",VERTEX,{"derivedFrom":[subQ1,subQ0]});Q30=makeQuery(id+"F0.imprint","IMPRINT",FACE,{"disambiguationData":[TD([[makeQuery(id+"F0.imprint","IMPRINT",EDGE,{"disambiguationData":[TD([[subQ2,1.0]])],"derivedFrom":subQ1}),1.0]])]});}
            var Q31;
            {var subQ0=sQuery(id+"F0.wireOp",EDGE,"E25");var subQ1=sQuery(id+"F0.wireOp",EDGE,"E14.MirrorCS");var subQ2=makeQuery(id+"F0.imprint","INTERSECT",VERTEX,{"derivedFrom":[subQ1,subQ0]});Q31=makeQuery(id+"F0.imprint","IMPRINT",FACE,{"disambiguationData":[TD([[makeQuery(id+"F0.imprint","IMPRINT",EDGE,{"disambiguationData":[TD([[subQ2,1.0]])],"derivedFrom":subQ1}),1.0]])]});}
            extrude(context, id + "F4", {"entities" : qUnion([Q0, Q1, Q2, Q3, Q4, Q5, Q6, Q7, Q8, Q9, Q10, Q11, Q12, Q13, Q14, Q15, Q16, Q17, Q18, Q19, Q20, Q21, Q22, Q23, Q24, Q25, Q26, Q27, Q28, Q29, Q30, Q31]), "operationType" : NewBodyOperationType.ADD, "depth" : 2.67 * mm});
        }
        {
            var Q0;
            Q0=makeQuery(id+"F4.opExtrude","CAP_EDGE",EDGE,{"disambiguationData":[OSD([sQuery(id+"F0.wireOp",EDGE,"E28")])],"isStart":false});
            var Q1;
            {var subQ0=sQuery(id+"F0.wireOp",EDGE,"E14.MirrorCS");Q1=makeQuery(id+"F4.opExtrude","CAP_EDGE",EDGE,{"disambiguationData":[OSD([subQ0]),TDD([makeQuery(id+"F0.imprint","IMPRINT",EDGE,{"disambiguationData":[TD([[makeQuery(id+"F0.imprint","INTERSECT",VERTEX,{"derivedFrom":[sQuery(id+"F0.wireOp",EDGE,"E3.right"),subQ0]}),-1.0]])],"derivedFrom":subQ0})])],"isStart":false});}
            var Q2;
            Q2=makeQuery(id+"F4.opExtrude","CAP_EDGE",EDGE,{"disambiguationData":[OSD([sQuery(id+"F0.wireOp",EDGE,"E4.top")])],"isStart":false});
            var Q3;
            {var subQ0=sQuery(id+"F0.wireOp",EDGE,"E14.MirrorCS");Q3=makeQuery(id+"F4.opExtrude","CAP_EDGE",EDGE,{"disambiguationData":[OSD([subQ0]),TDD([makeQuery(id+"F0.imprint","IMPRINT",EDGE,{"disambiguationData":[TD([[makeQuery(id+"F0.imprint","INTERSECT",VERTEX,{"derivedFrom":[sQuery(id+"F0.wireOp",EDGE,"E4.left"),subQ0]}),1.0]])],"derivedFrom":subQ0})])],"isStart":false});}
            var Q4;
            {var subQ0=sQuery(id+"F0.wireOp",EDGE,"E14.MirrorCS");Q4=makeQuery(id+"F4.opExtrude","CAP_EDGE",EDGE,{"disambiguationData":[OSD([subQ0]),TDD([makeQuery(id+"F0.imprint","IMPRINT",EDGE,{"disambiguationData":[TD([[makeQuery(id+"F0.imprint","INTERSECT",VERTEX,{"derivedFrom":[sQuery(id+"F0.wireOp",EDGE,"E5.left"),subQ0]}),1.0]])],"derivedFrom":subQ0})])],"isStart":false});}
            var Q5;
            Q5=makeQuery(id+"F4.opExtrude","CAP_EDGE",EDGE,{"disambiguationData":[OSD([sQuery(id+"F0.wireOp",EDGE,"E5.top")])],"isStart":false});
            var Q6;
            Q6=makeQuery(id+"F4.opExtrude","CAP_EDGE",EDGE,{"disambiguationData":[OSD([sQuery(id+"F0.wireOp",EDGE,"E6.top")])],"isStart":false});
            var Q7;
            {var subQ0=sQuery(id+"F0.wireOp",EDGE,"E14.MirrorCS");Q7=makeQuery(id+"F4.opExtrude","CAP_EDGE",EDGE,{"disambiguationData":[OSD([subQ0]),TDD([makeQuery(id+"F0.imprint","IMPRINT",EDGE,{"disambiguationData":[TD([[makeQuery(id+"F0.imprint","INTERSECT",VERTEX,{"derivedFrom":[sQuery(id+"F0.wireOp",EDGE,"E6.left"),subQ0]}),1.0]])],"derivedFrom":subQ0})])],"isStart":false});}
            var Q8;
            Q8=makeQuery(id+"F4.opExtrude","CAP_EDGE",EDGE,{"disambiguationData":[OSD([sQuery(id+"F0.wireOp",EDGE,"E19.MirrorCS")])],"isStart":false});
            var Q9;
            Q9=makeQuery(id+"F4.opExtrude","CAP_EDGE",EDGE,{"disambiguationData":[OSD([sQuery(id+"F0.wireOp",EDGE,"E20.MirrorCS")])],"isStart":false});
            var Q10;
            Q10=makeQuery(id+"F4.opExtrude","CAP_EDGE",EDGE,{"disambiguationData":[OSD([sQuery(id+"F0.wireOp",EDGE,"E16.MirrorCS")])],"isStart":false});
            var Q11;
            {var subQ0=sQuery(id+"F0.wireOp",EDGE,"E14.MirrorCS");Q11=makeQuery(id+"F4.opExtrude","CAP_EDGE",EDGE,{"disambiguationData":[OSD([subQ0]),TDD([makeQuery(id+"F0.imprint","IMPRINT",EDGE,{"disambiguationData":[TD([[makeQuery(id+"F0.imprint","INTERSECT",VERTEX,{"derivedFrom":[subQ0,sQuery(id+"F0.wireOp",EDGE,"E15.MirrorCS")]}),-1.0]])],"derivedFrom":subQ0})])],"isStart":false});}
            var Q12;
            {var subQ0=sQuery(id+"F0.wireOp",EDGE,"E14.MirrorCS");Q12=makeQuery(id+"F4.opExtrude","CAP_EDGE",EDGE,{"disambiguationData":[OSD([subQ0]),TDD([makeQuery(id+"F0.imprint","IMPRINT",EDGE,{"disambiguationData":[TD([[makeQuery(id+"F0.imprint","INTERSECT",VERTEX,{"derivedFrom":[sQuery(id+"F0.wireOp",EDGE,"E9.MirrorCS"),subQ0]}),1.0]])],"derivedFrom":subQ0})])],"isStart":false});}
            var Q13;
            Q13=makeQuery(id+"F4.opExtrude","CAP_EDGE",EDGE,{"disambiguationData":[OSD([sQuery(id+"F0.wireOp",EDGE,"E8.MirrorCS")])],"isStart":false});
            var Q14;
            Q14=makeQuery(id+"F4.opExtrude","CAP_EDGE",EDGE,{"disambiguationData":[OSD([sQuery(id+"F0.wireOp",EDGE,"E27")])],"isStart":false});
            var Q15;
            {var subQ0=sQuery(id+"F0.wireOp",EDGE,"E14.MirrorCS");Q15=makeQuery(id+"F4.opExtrude","CAP_EDGE",EDGE,{"disambiguationData":[OSD([subQ0]),TDD([makeQuery(id+"F0.imprint","IMPRINT",EDGE,{"disambiguationData":[TD([[makeQuery(id+"F0.imprint","INTERSECT",VERTEX,{"derivedFrom":[sQuery(id+"F0.wireOp",EDGE,"E12.MirrorCS"),subQ0]}),1.0]])],"derivedFrom":subQ0})])],"isStart":false});}
            var Q16;
            Q16=makeQuery(id+"F4.opExtrude","CAP_EDGE",EDGE,{"disambiguationData":[OSD([sQuery(id+"F0.wireOp",EDGE,"E25")])],"isStart":false});
            var Q17;
            Q17=makeQuery(id+"F4.opExtrude","CAP_EDGE",EDGE,{"disambiguationData":[OSD([sQuery(id+"F0.wireOp",EDGE,"E3.right")])],"isStart":false});
            var Q18;
            Q18=makeQuery(id+"F4.opExtrude","CAP_EDGE",EDGE,{"disambiguationData":[OSD([sQuery(id+"F0.wireOp",EDGE,"E4.left")])],"isStart":false});
            var Q19;
            Q19=makeQuery(id+"F4.opExtrude","CAP_EDGE",EDGE,{"disambiguationData":[OSD([sQuery(id+"F0.wireOp",EDGE,"E4.right")])],"isStart":false});
            var Q20;
            Q20=makeQuery(id+"F4.opExtrude","CAP_EDGE",EDGE,{"disambiguationData":[OSD([sQuery(id+"F0.wireOp",EDGE,"E5.left")])],"isStart":false});
            var Q21;
            Q21=makeQuery(id+"F4.opExtrude","CAP_EDGE",EDGE,{"disambiguationData":[OSD([sQuery(id+"F0.wireOp",EDGE,"E5.right")])],"isStart":false});
            var Q22;
            Q22=makeQuery(id+"F4.opExtrude","CAP_EDGE",EDGE,{"disambiguationData":[OSD([sQuery(id+"F0.wireOp",EDGE,"E6.left")])],"isStart":false});
            var Q23;
            Q23=makeQuery(id+"F4.opExtrude","CAP_EDGE",EDGE,{"disambiguationData":[OSD([sQuery(id+"F0.wireOp",EDGE,"E6.right")])],"isStart":false});
            var Q24;
            Q24=makeQuery(id+"F4.opExtrude","CAP_EDGE",EDGE,{"disambiguationData":[OSD([sQuery(id+"F0.wireOp",EDGE,"E21.MirrorCS")])],"isStart":false});
            var Q25;
            Q25=makeQuery(id+"F4.opExtrude","CAP_EDGE",EDGE,{"disambiguationData":[OSD([sQuery(id+"F0.wireOp",EDGE,"E18.MirrorCS")])],"isStart":false});
            var Q26;
            Q26=makeQuery(id+"F4.opExtrude","CAP_EDGE",EDGE,{"disambiguationData":[OSD([sQuery(id+"F0.wireOp",EDGE,"E17.MirrorCS")])],"isStart":false});
            var Q27;
            Q27=makeQuery(id+"F4.opExtrude","CAP_EDGE",EDGE,{"disambiguationData":[OSD([sQuery(id+"F0.wireOp",EDGE,"E15.MirrorCS")])],"isStart":false});
            var Q28;
            Q28=makeQuery(id+"F4.opExtrude","CAP_EDGE",EDGE,{"disambiguationData":[OSD([sQuery(id+"F0.wireOp",EDGE,"E9.MirrorCS")])],"isStart":false});
            var Q29;
            Q29=makeQuery(id+"F4.opExtrude","CAP_EDGE",EDGE,{"disambiguationData":[OSD([sQuery(id+"F0.wireOp",EDGE,"E10.MirrorCS")])],"isStart":false});
            var Q30;
            Q30=makeQuery(id+"F4.opExtrude","CAP_EDGE",EDGE,{"disambiguationData":[OSD([sQuery(id+"F0.wireOp",EDGE,"E12.MirrorCS")])],"isStart":false});
            var Q31;
            Q31=makeQuery(id+"F4.opExtrude","CAP_EDGE",EDGE,{"disambiguationData":[OSD([sQuery(id+"F0.wireOp",EDGE,"E26.MirrorCS")])],"isStart":false});
            chamfer(context, id + "F5", {"entities" : qUnion([Q0, Q1, Q2, Q3, Q4, Q5, Q6, Q7, Q8, Q9, Q10, Q11, Q12, Q13, Q14, Q15, Q16, Q17, Q18, Q19, Q20, Q21, Q22, Q23, Q24, Q25, Q26, Q27, Q28, Q29, Q30, Q31]), "width" : 0.25 * mm, "tangentPropagation" : true});
        }
        {
            var Q0;
            Q0=makeQuery(id+"F4.boolean.opBoolean","SPLIT",FACE,{"disambiguationData":[TD([makeQuery(id+"F4.opExtrude","SWEPT_FACE",FACE,{"disambiguationData":[OSD([sQuery(id+"F0.wireOp",EDGE,"E29")])]})])],"derivedFrom":makeQuery(id+"F1.opExtrude","CAP_FACE",FACE,{"disambiguationData":[OSD([sQuery(id+"F0.wireOp",EDGE,"E0.bottom"),sQuery(id+"F0.wireOp",EDGE,"E0.top"),sQuery(id+"F0.wireOp",EDGE,"E0.left"),sQuery(id+"F0.wireOp",EDGE,"E0.right"),sQuery(id+"F0.wireOp",EDGE,"E1"),sQuery(id+"F0.wireOp",EDGE,"E7.MirrorC"),sQuery(id+"F0.wireOp",EDGE,"E3.left")])],"isStart":false})});
            var Q1;
            Q1=makeQuery(id+"F4.boolean.opBoolean","SPLIT",FACE,{"disambiguationData":[TD([makeQuery(id+"F4.opExtrude","SWEPT_FACE",FACE,{"disambiguationData":[OSD([sQuery(id+"F0.wireOp",EDGE,"E30")])]})])],"derivedFrom":makeQuery(id+"F1.opExtrude","CAP_FACE",FACE,{"disambiguationData":[OSD([sQuery(id+"F0.wireOp",EDGE,"E0.bottom"),sQuery(id+"F0.wireOp",EDGE,"E0.top"),sQuery(id+"F0.wireOp",EDGE,"E0.left"),sQuery(id+"F0.wireOp",EDGE,"E0.right"),sQuery(id+"F0.wireOp",EDGE,"E1"),sQuery(id+"F0.wireOp",EDGE,"E7.MirrorC"),sQuery(id+"F0.wireOp",EDGE,"E3.left")])],"isStart":false})});
            var Q2;
            Q2=makeQuery(id+"F4.boolean.opBoolean","SPLIT",FACE,{"disambiguationData":[TD([makeQuery(id+"F4.opExtrude","SWEPT_FACE",FACE,{"disambiguationData":[OSD([sQuery(id+"F0.wireOp",EDGE,"E31")])]})])],"derivedFrom":makeQuery(id+"F1.opExtrude","CAP_FACE",FACE,{"disambiguationData":[OSD([sQuery(id+"F0.wireOp",EDGE,"E0.bottom"),sQuery(id+"F0.wireOp",EDGE,"E0.top"),sQuery(id+"F0.wireOp",EDGE,"E0.left"),sQuery(id+"F0.wireOp",EDGE,"E0.right"),sQuery(id+"F0.wireOp",EDGE,"E1"),sQuery(id+"F0.wireOp",EDGE,"E7.MirrorC"),sQuery(id+"F0.wireOp",EDGE,"E3.left")])],"isStart":false})});
            var Q3;
            Q3=makeQuery(id+"F4.boolean.opBoolean","SPLIT",FACE,{"disambiguationData":[TD([makeQuery(id+"F4.opExtrude","SWEPT_FACE",FACE,{"disambiguationData":[OSD([sQuery(id+"F0.wireOp",EDGE,"E32")])]})])],"derivedFrom":makeQuery(id+"F1.opExtrude","CAP_FACE",FACE,{"disambiguationData":[OSD([sQuery(id+"F0.wireOp",EDGE,"E0.bottom"),sQuery(id+"F0.wireOp",EDGE,"E0.top"),sQuery(id+"F0.wireOp",EDGE,"E0.left"),sQuery(id+"F0.wireOp",EDGE,"E0.right"),sQuery(id+"F0.wireOp",EDGE,"E1"),sQuery(id+"F0.wireOp",EDGE,"E7.MirrorC"),sQuery(id+"F0.wireOp",EDGE,"E3.left")])],"isStart":false})});
            var Q4;
            Q4=makeQuery(id+"F4.boolean.opBoolean","SPLIT",FACE,{"disambiguationData":[TD([makeQuery(id+"F4.opExtrude","SWEPT_FACE",FACE,{"disambiguationData":[OSD([sQuery(id+"F0.wireOp",EDGE,"E33.MirrorC")])]})])],"derivedFrom":makeQuery(id+"F1.opExtrude","CAP_FACE",FACE,{"disambiguationData":[OSD([sQuery(id+"F0.wireOp",EDGE,"E0.bottom"),sQuery(id+"F0.wireOp",EDGE,"E0.top"),sQuery(id+"F0.wireOp",EDGE,"E0.left"),sQuery(id+"F0.wireOp",EDGE,"E0.right"),sQuery(id+"F0.wireOp",EDGE,"E1"),sQuery(id+"F0.wireOp",EDGE,"E7.MirrorC"),sQuery(id+"F0.wireOp",EDGE,"E3.left")])],"isStart":false})});
            var Q5;
            Q5=makeQuery(id+"F4.boolean.opBoolean","SPLIT",FACE,{"disambiguationData":[TD([makeQuery(id+"F4.opExtrude","SWEPT_FACE",FACE,{"disambiguationData":[OSD([sQuery(id+"F0.wireOp",EDGE,"E34.MirrorC")])]})])],"derivedFrom":makeQuery(id+"F1.opExtrude","CAP_FACE",FACE,{"disambiguationData":[OSD([sQuery(id+"F0.wireOp",EDGE,"E0.bottom"),sQuery(id+"F0.wireOp",EDGE,"E0.top"),sQuery(id+"F0.wireOp",EDGE,"E0.left"),sQuery(id+"F0.wireOp",EDGE,"E0.right"),sQuery(id+"F0.wireOp",EDGE,"E1"),sQuery(id+"F0.wireOp",EDGE,"E7.MirrorC"),sQuery(id+"F0.wireOp",EDGE,"E3.left")])],"isStart":false})});
            var Q6;
            Q6=makeQuery(id+"F4.boolean.opBoolean","SPLIT",FACE,{"disambiguationData":[TD([makeQuery(id+"F4.opExtrude","SWEPT_FACE",FACE,{"disambiguationData":[OSD([sQuery(id+"F0.wireOp",EDGE,"E35.MirrorC")])]})])],"derivedFrom":makeQuery(id+"F1.opExtrude","CAP_FACE",FACE,{"disambiguationData":[OSD([sQuery(id+"F0.wireOp",EDGE,"E0.bottom"),sQuery(id+"F0.wireOp",EDGE,"E0.top"),sQuery(id+"F0.wireOp",EDGE,"E0.left"),sQuery(id+"F0.wireOp",EDGE,"E0.right"),sQuery(id+"F0.wireOp",EDGE,"E1"),sQuery(id+"F0.wireOp",EDGE,"E7.MirrorC"),sQuery(id+"F0.wireOp",EDGE,"E3.left")])],"isStart":false})});
            var Q7;
            Q7=makeQuery(id+"F4.boolean.opBoolean","SPLIT",FACE,{"disambiguationData":[TD([makeQuery(id+"F4.opExtrude","SWEPT_FACE",FACE,{"disambiguationData":[OSD([sQuery(id+"F0.wireOp",EDGE,"E36.MirrorC")])]})])],"derivedFrom":makeQuery(id+"F1.opExtrude","CAP_FACE",FACE,{"disambiguationData":[OSD([sQuery(id+"F0.wireOp",EDGE,"E0.bottom"),sQuery(id+"F0.wireOp",EDGE,"E0.top"),sQuery(id+"F0.wireOp",EDGE,"E0.left"),sQuery(id+"F0.wireOp",EDGE,"E0.right"),sQuery(id+"F0.wireOp",EDGE,"E1"),sQuery(id+"F0.wireOp",EDGE,"E7.MirrorC"),sQuery(id+"F0.wireOp",EDGE,"E3.left")])],"isStart":false})});
            extrude(context, id + "F6", {"entities" : qUnion([Q0, Q1, Q2, Q3, Q4, Q5, Q6, Q7]), "operationType" : NewBodyOperationType.ADD, "depth" : 1.78 * mm});
        }
    });
